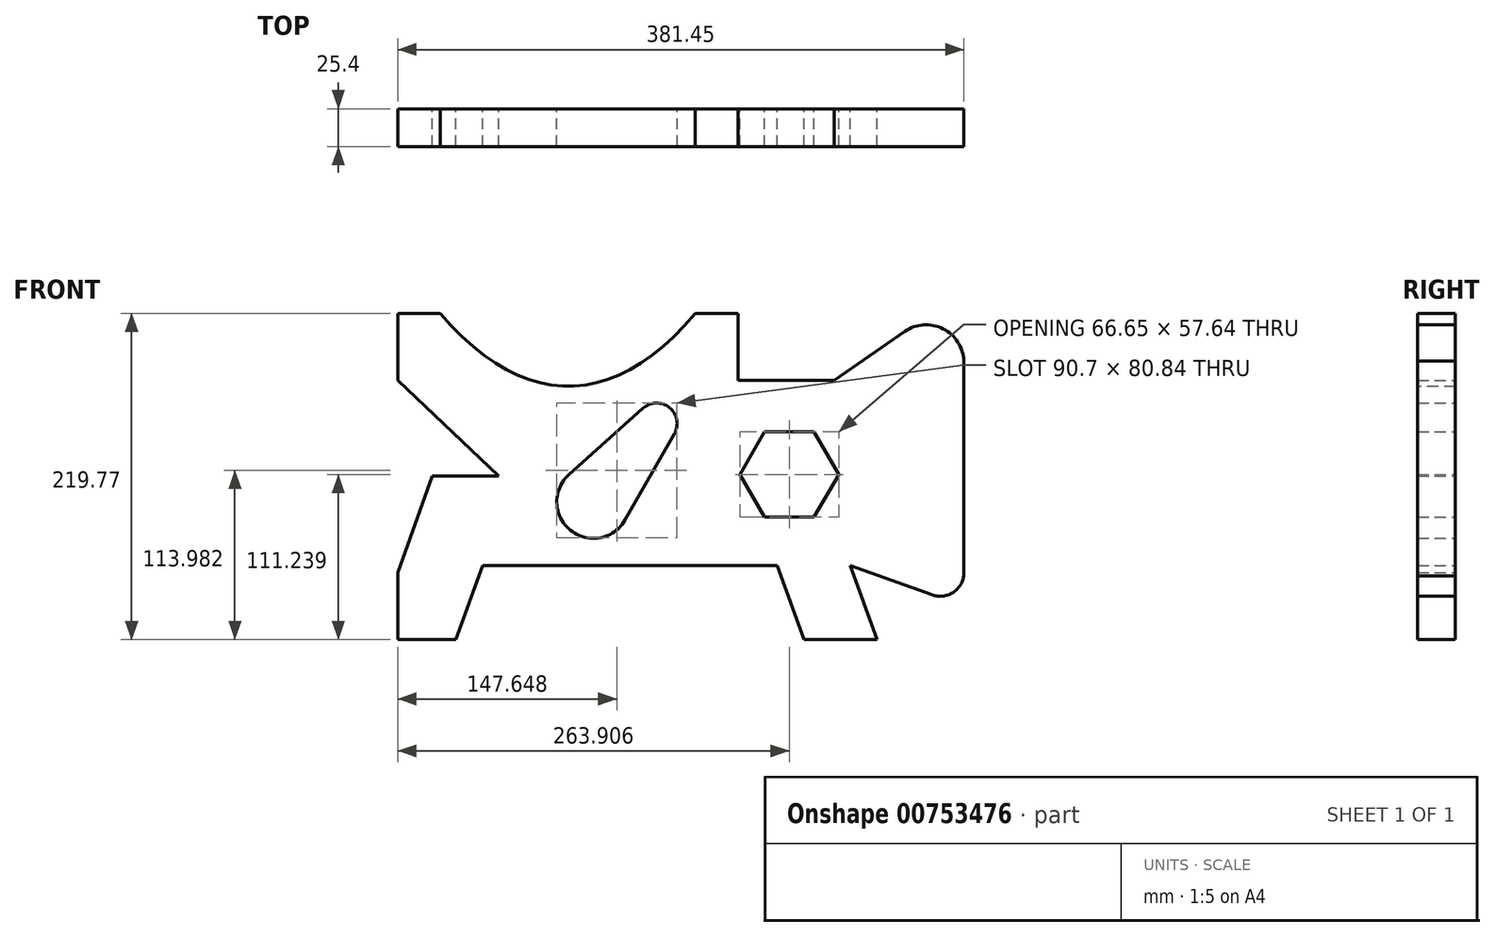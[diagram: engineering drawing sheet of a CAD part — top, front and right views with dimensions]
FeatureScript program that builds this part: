
annotation { "Feature Type Name" : "Feature", "Feature Type Description" : "" }
export const myFeature = defineFeature(function(context is Context, id is Id, definition is map)
    precondition{}
    {
        {
            var Q0;
            Q0=qCreatedBy(makeId("Front.planeOp"),FACE);
            var sketch = newSketch(context, id + "F0", { "sketchPlane" : qUnion([Q0])});
            skLineSegment(sketch, "E0", {"start": v(-205.82, 105.56) * mm, "end": v(-177, 105.56) * mm});
            skFitSpline(sketch, "E1", {"points": [v(-177, 105.56) * mm, v(-5.41, 105.56) * mm], "startDerivative": vector(166.18, -197.25) * mm, "endDerivative": vector(163.48, 195.9) * mm});
            skLineSegment(sketch, "E2", {"start": v(-5.41, 105.56) * mm, "end": v(23.4, 105.56) * mm});
            skLineSegment(sketch, "E3", {"start": v(23.4, 105.56) * mm, "end": v(23.4, 60.53) * mm});
            skLineSegment(sketch, "E4", {"start": v(-205.82, 105.56) * mm, "end": v(-205.82, 60.53) * mm});
            skLineSegment(sketch, "E5", {"start": v(23.4, 60.53) * mm, "end": v(88.26, 60.53) * mm});
            skLineSegment(sketch, "E6", {"start": v(88.26, 60.53) * mm, "end": v(136, 93.4) * mm});
            skLineSegment(sketch, "E7", {"start": v(-205.82, 60.53) * mm, "end": v(-137.82, -3.87) * mm});
            skLineSegment(sketch, "E8", {"start": v(-137.82, -3.87) * mm, "end": v(-182.4, -3.87) * mm});
            skLineSegment(sketch, "E9", {"start": v(-182.4, -3.87) * mm, "end": v(-205.82, -69.17) * mm});
            skLineSegment(sketch, "E10", {"start": v(-205.82, -69.17) * mm, "end": v(-205.82, -114.2) * mm});
            skLineSegment(sketch, "E11", {"start": v(-205.82, -114.2) * mm, "end": v(-166.64, -114.2) * mm});
            skLineSegment(sketch, "E12", {"start": v(-166.64, -114.2) * mm, "end": v(-148.63, -64.22) * mm});
            skLineSegment(sketch, "E13", {"start": v(-148.63, -64.22) * mm, "end": v(49.98, -64.22) * mm});
            skLineSegment(sketch, "E14", {"start": v(49.98, -64.22) * mm, "end": v(68, -114.2) * mm});
            skLineSegment(sketch, "E15", {"start": v(68, -114.2) * mm, "end": v(117.08, -114.2) * mm});
            skLineSegment(sketch, "E16", {"start": v(117.08, -114.2) * mm, "end": v(99.07, -64.22) * mm});
            skLineSegment(sketch, "E17", {"start": v(99.07, -64.22) * mm, "end": v(154.2, -84.08) * mm});
            skArc(sketch, "E18", {"start": v(154.2, -84.08) * mm, "mid": v(167.89, -82.8) * mm, "end": v(175.63, -71.42) * mm});
            skArc(sketch, "E19", {"start": v(136, 93.4) * mm, "mid": v(161.66, 95.2) * mm, "end": v(175.63, 73.59) * mm});
            skLineSegment(sketch, "E20", {"start": v(175.63, 73.59) * mm, "end": v(175.63, -71.42) * mm});
            skLineSegment(sketch, "E21", {"start": v(41.42, 25.85) * mm, "end": v(24.76, -2.97) * mm});
            skLineSegment(sketch, "E22", {"start": v(24.76, -2.97) * mm, "end": v(41.42, -31.8) * mm});
            skLineSegment(sketch, "E23", {"start": v(41.42, -31.8) * mm, "end": v(74.75, -31.8) * mm});
            skLineSegment(sketch, "E24", {"start": v(74.75, -31.8) * mm, "end": v(91.41, -2.97) * mm});
            skLineSegment(sketch, "E25", {"start": v(91.41, -2.97) * mm, "end": v(74.75, 25.85) * mm});
            skLineSegment(sketch, "E26", {"start": v(74.75, 25.85) * mm, "end": v(41.42, 25.85) * mm});
            skArc(sketch, "E27", {"start": v(-40.54, 41.61) * mm, "mid": v(-22.68, 42.06) * mm, "end": v(-19.37, 24.5) * mm});
            skLineSegment(sketch, "E28", {"start": v(-19.37, 24.5) * mm, "end": v(-52.52, -33.57) * mm});
            skLineSegment(sketch, "E29", {"start": v(-40.54, 41.61) * mm, "end": v(-90.42, -3) * mm});
            skArc(sketch, "E30", {"start": v(-52.52, -33.57) * mm, "mid": v(-89.43, -40.54) * mm, "end": v(-90.42, -3) * mm});
            skSolve(sketch);
        }
        {
            var Q0;
            Q0=makeQuery(id+"F0.imprint","IMPRINT",FACE,{"disambiguationData":[TD([[makeQuery(id+"F0.imprint","IMPRINT",EDGE,{"derivedFrom":sQuery(id+"F0.wireOp",EDGE,"E0")}),-1.0]])]});
            extrude(context, id + "F1", {"entities" : qUnion([Q0]), "endBound" : BoundingType.SYMMETRIC, "depth" : 25.4 * mm, "offsetDistance" : 25.4 * mm});
        }
    });
